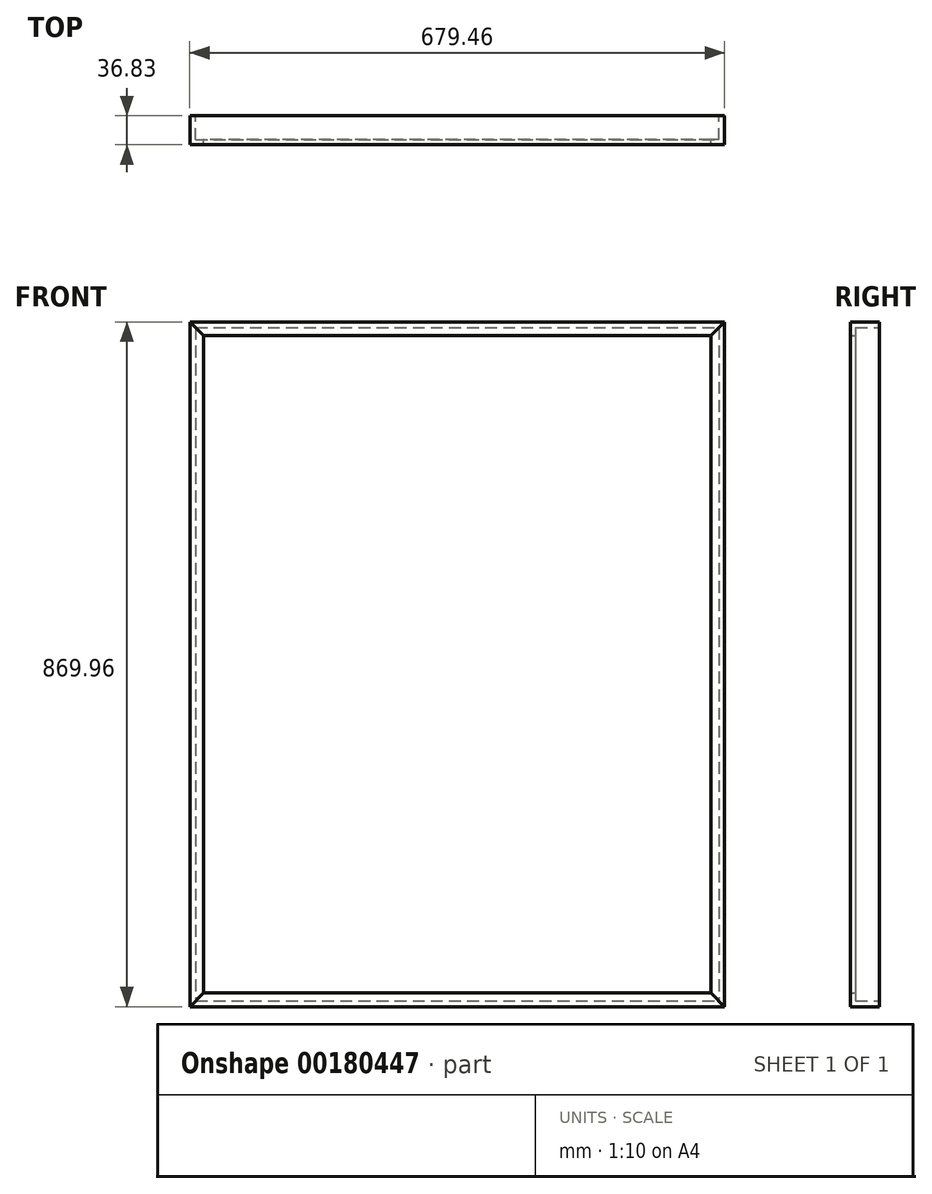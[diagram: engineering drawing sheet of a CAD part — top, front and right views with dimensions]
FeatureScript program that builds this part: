
annotation { "Feature Type Name" : "Feature", "Feature Type Description" : "" }
export const myFeature = defineFeature(function(context is Context, id is Id, definition is map)
    precondition{}
    {
        {
            var Q0;
            Q0=qCreatedBy(makeId("Front.planeOp"),FACE);
            var sketch = newSketch(context, id + "F0", { "sketchPlane" : qUnion([Q0])});
            skLineSegment(sketch, "E0.bottom", {"start": v(-339.73, -434.98) * mm, "end": v(339.73, -434.98) * mm});
            skLineSegment(sketch, "E0.top", {"start": v(-339.73, 434.98) * mm, "end": v(339.73, 434.98) * mm});
            skLineSegment(sketch, "E0.left", {"start": v(-339.73, -434.98) * mm, "end": v(-339.73, 434.98) * mm});
            skLineSegment(sketch, "E0.right", {"start": v(339.73, -434.98) * mm, "end": v(339.73, 434.98) * mm});
            skPoint(sketch, "E0.middle", {"position": v(0, 0) * mm});
            skLineSegment(sketch, "E1.bottom", {"start": v(322.33, 417.58) * mm, "end": v(-322.33, 417.58) * mm});
            skLineSegment(sketch, "E1.top", {"start": v(322.33, -417.58) * mm, "end": v(-322.33, -417.58) * mm});
            skLineSegment(sketch, "E1.left", {"start": v(322.33, 417.58) * mm, "end": v(322.33, -417.58) * mm});
            skLineSegment(sketch, "E1.right", {"start": v(-322.33, 417.58) * mm, "end": v(-322.33, -417.58) * mm});
            skSolve(sketch);
        }
        {
            var Q0;
            Q0=makeQuery(id+"F0.imprint","IMPRINT",FACE,{"disambiguationData":[TD([[makeQuery(id+"F0.imprint","IMPRINT",EDGE,{"derivedFrom":sQuery(id+"F0.wireOp",EDGE,"E1.bottom")}),1.0]])]});
            var sketch = newSketch(context, id + "F1", { "sketchPlane" : qUnion([Q0])});
            skLineSegment(sketch, "E2.0", {"start": v(-339.73, -434.98) * mm, "end": v(-339.73, 434.98) * mm});
            skLineSegment(sketch, "E3.0", {"start": v(339.73, -434.98) * mm, "end": v(339.73, 434.98) * mm});
            skLineSegment(sketch, "E4.0", {"start": v(-322.33, 417.58) * mm, "end": v(-322.33, -417.58) * mm});
            skLineSegment(sketch, "E5.0", {"start": v(322.33, 417.58) * mm, "end": v(322.33, -417.58) * mm});
            skLineSegment(sketch, "E6", {"start": v(-339.73, 434.98) * mm, "end": v(-322.33, 417.58) * mm});
            skLineSegment(sketch, "E7", {"start": v(339.73, 434.98) * mm, "end": v(322.33, 417.58) * mm});
            skLineSegment(sketch, "E8", {"start": v(-322.33, -417.58) * mm, "end": v(-339.73, -434.98) * mm});
            skLineSegment(sketch, "E9", {"start": v(322.33, -417.58) * mm, "end": v(339.73, -434.98) * mm});
            skSolve(sketch);
        }
        {
            var Q0;
            Q0=qSketchRegion(id+"F1",true);
            extrude(context, id + "F2", {"entities" : qUnion([Q0]), "depth" : 36.83 * mm});
        }
        {
            var Q0;
            Q0=qCreatedBy(makeId("Front.planeOp"),FACE);
            var sketch = newSketch(context, id + "F3", { "sketchPlane" : qUnion([Q0])});
            skLineSegment(sketch, "E10.0", {"start": v(-339.73, 434.98) * mm, "end": v(339.73, 434.98) * mm});
            skLineSegment(sketch, "E11.0", {"start": v(322.33, 417.58) * mm, "end": v(-322.33, 417.58) * mm});
            skLineSegment(sketch, "E12.0", {"start": v(-339.73, 434.98) * mm, "end": v(-322.33, 417.58) * mm});
            skLineSegment(sketch, "E13.0", {"start": v(339.73, 434.98) * mm, "end": v(322.33, 417.58) * mm});
            skLineSegment(sketch, "E14.0", {"start": v(-339.73, -434.98) * mm, "end": v(339.73, -434.98) * mm});
            skLineSegment(sketch, "E15.0", {"start": v(322.33, -417.58) * mm, "end": v(-322.33, -417.58) * mm});
            skLineSegment(sketch, "E16.0", {"start": v(-322.33, -417.58) * mm, "end": v(-339.73, -434.98) * mm});
            skLineSegment(sketch, "E17.0", {"start": v(322.33, -417.58) * mm, "end": v(339.73, -434.98) * mm});
            skSolve(sketch);
        }
        {
            var Q0;
            Q0=qSketchRegion(id+"F3",true);
            var Q1;
            Q1=makeQuery(id+"F2.opExtrude","CAP_FACE",FACE,{"disambiguationData":[OSD([sQuery(id+"F1.wireOp",EDGE,"E2.0"),sQuery(id+"F1.wireOp",EDGE,"E4.0"),sQuery(id+"F1.wireOp",EDGE,"E6"),sQuery(id+"F1.wireOp",EDGE,"E8")])],"isStart":false});
            extrude(context, id + "F4", {"entities" : qUnion([Q0]), "endBound" : BoundingType.UP_TO_SURFACE, "endBoundEntityFace" : qUnion([Q1]), "depth" : 25.4 * mm});
        }
        {
            var Q0;
            Q0=makeQuery(id+"F0.imprint","IMPRINT",FACE,{"disambiguationData":[TD([[makeQuery(id+"F0.imprint","IMPRINT",EDGE,{"derivedFrom":sQuery(id+"F0.wireOp",EDGE,"E0.bottom")}),1.0]])]});
            var sketch = newSketch(context, id + "F5", { "sketchPlane" : qUnion([Q0])});
            skLineSegment(sketch, "E18.bottom", {"start": v(-332.49, 427.74) * mm, "end": v(332.49, 427.74) * mm});
            skLineSegment(sketch, "E18.top", {"start": v(-332.49, -427.74) * mm, "end": v(332.49, -427.74) * mm});
            skLineSegment(sketch, "E18.left", {"start": v(-332.49, 427.74) * mm, "end": v(-332.49, -427.74) * mm});
            skLineSegment(sketch, "E18.right", {"start": v(332.49, 427.74) * mm, "end": v(332.49, -427.74) * mm});
            skPoint(sketch, "E18.middle", {"position": v(0, 0) * mm});
            skSolve(sketch);
        }
        {
            var Q0;
            Q0=qSketchRegion(id+"F5",true);
            extrude(context, id + "F6", {"entities" : qUnion([Q0]), "operationType" : NewBodyOperationType.REMOVE, "depth" : 30.48 * mm});
        }
    });
